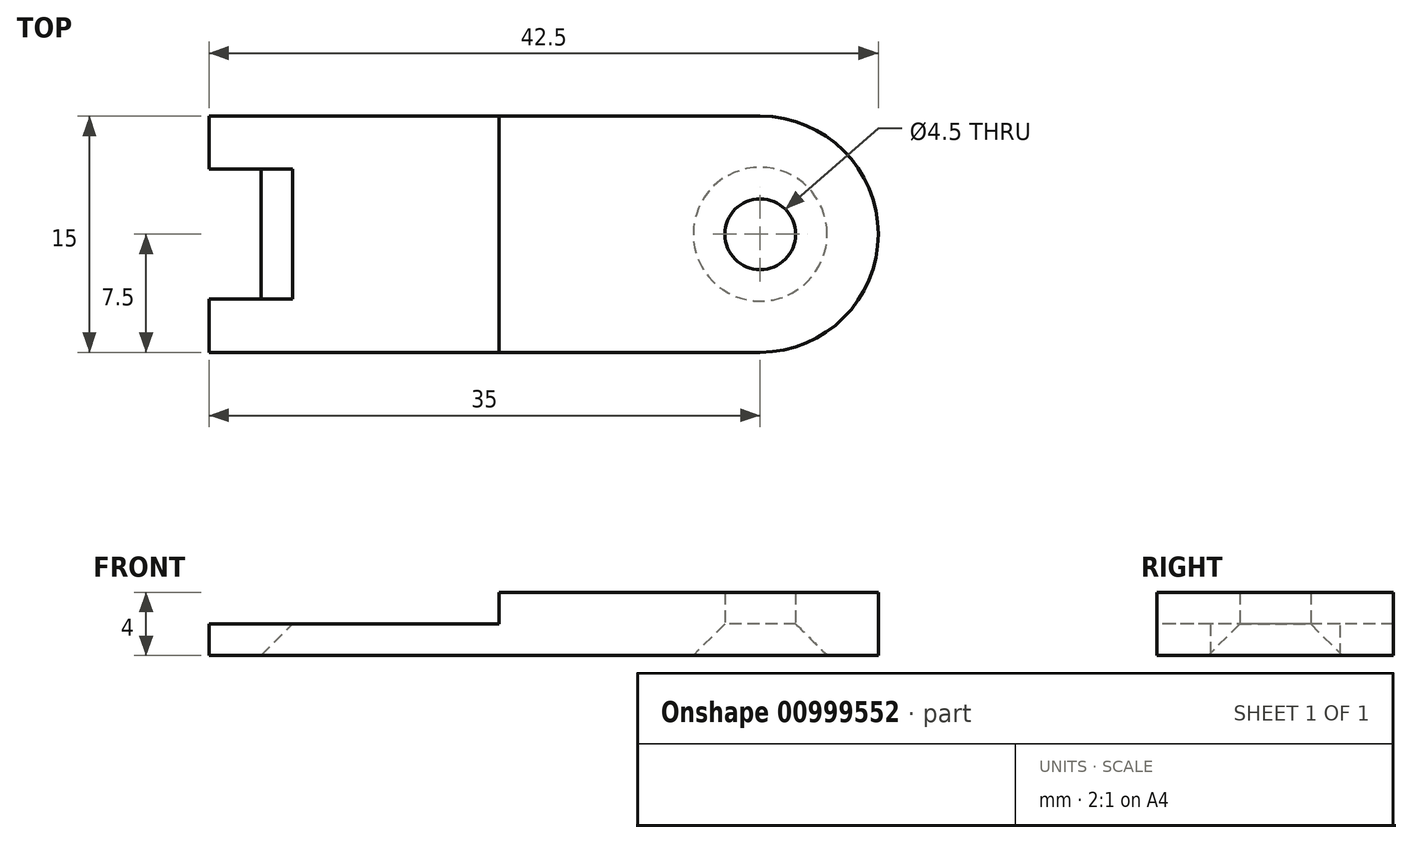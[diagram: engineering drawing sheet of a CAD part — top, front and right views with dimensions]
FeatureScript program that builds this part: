
annotation { "Feature Type Name" : "Feature", "Feature Type Description" : "" }
export const myFeature = defineFeature(function(context is Context, id is Id, definition is map)
    precondition{}
    {
        {
            var Q0;
            Q0=qCreatedBy(makeId("Top.planeOp"),FACE);
            var sketch = newSketch(context, id + "F0", { "sketchPlane" : qUnion([Q0])});
            skLineSegment(sketch, "E0.bottom", {"start": v(-21, 7.5) * mm, "end": v(14, 7.5) * mm});
            skLineSegment(sketch, "E0.top", {"start": v(-21, -7.5) * mm, "end": v(14, -7.5) * mm});
            skLineSegment(sketch, "E0.left", {"start": v(-21, 7.5) * mm, "end": v(-21, 4.12) * mm});
            skPoint(sketch, "E0.middle", {"position": v(0, 0) * mm});
            skCircle(sketch, "E1", {"center": v(14, 0) * mm, "radius": 2.25 * mm});
            skLineSegment(sketch, "E2.bottom", {"start": v(-17.7, 4.12) * mm, "end": v(-21, 4.12) * mm});
            skLineSegment(sketch, "E2.top", {"start": v(-17.7, -4.12) * mm, "end": v(-24.3, -4.12) * mm});
            skLineSegment(sketch, "E2.left", {"start": v(-17.7, 4.12) * mm, "end": v(-17.7, -4.13) * mm});
            skPoint(sketch, "E2.middle", {"position": v(-21, 0) * mm});
            skLineSegment(sketch, "E3.bottom", {"start": v(-2.6, 7.5) * mm, "end": v(-21, 7.5) * mm});
            skLineSegment(sketch, "E3.top", {"start": v(-2.6, -7.5) * mm, "end": v(-21, -7.5) * mm});
            skLineSegment(sketch, "E3.left", {"start": v(-2.6, 7.5) * mm, "end": v(-2.6, -7.5) * mm});
            skPoint(sketch, "E2.right.start.orphan", {"position": v(-24.3, 4.12) * mm});
            skLineSegment(sketch, "E4.trimOffspring", {"start": v(-21, -4.12) * mm, "end": v(-21, -7.5) * mm});
            skPoint(sketch, "E3.right.start.orphan", {"position": v(-39.4, 7.5) * mm});
            skPoint(sketch, "E5.orphan", {"position": v(-39.4, -7.5) * mm});
            skPoint(sketch, "E6.orphan", {"position": v(-2.6, 0) * mm});
            skArc(sketch, "E7", {"start": v(14, -7.5) * mm, "mid": v(21.5, 0) * mm, "end": v(14, 7.5) * mm});
            skPoint(sketch, "E8.orphan", {"position": v(21, 7.5) * mm});
            skPoint(sketch, "E9.orphan", {"position": v(21, -7.5) * mm});
            skSolve(sketch);
        }
        {
            var Q0;
            Q0=makeQuery(id+"F0.imprint","IMPRINT",FACE,{"disambiguationData":[TD([[makeQuery(id+"F0.imprint","IMPRINT",EDGE,{"derivedFrom":sQuery(id+"F0.wireOp",EDGE,"E0.bottom")}),-1.0]])]});
            extrude(context, id + "F1", {"entities" : qUnion([Q0]), "depth" : 4 * mm, "offsetDistance" : 25 * mm});
        }
        {
            var Q0;
            Q0=makeQuery(id+"F0.imprint","IMPRINT",FACE,{"disambiguationData":[TD([[makeQuery(id+"F0.imprint","IMPRINT",EDGE,{"derivedFrom":sQuery(id+"F0.wireOp",EDGE,"E0.left")}),1.0]])]});
            extrude(context, id + "F2", {"entities" : qUnion([Q0]), "operationType" : NewBodyOperationType.ADD, "depth" : 2 * mm, "offsetDistance" : 25 * mm});
        }
        {
            var Q0;
            Q0=makeQuery(id+"F1.opExtrude","CAP_EDGE",EDGE,{"disambiguationData":[OSD([sQuery(id+"F0.wireOp",EDGE,"E1")])],"isStart":true});
            var Q1;
            Q1=makeQuery(id+"F2.opExtrude","CAP_EDGE",EDGE,{"disambiguationData":[OSD([sQuery(id+"F0.wireOp",EDGE,"E2.left")])],"isStart":false});
            chamfer(context, id + "F3", {"entities" : qUnion([Q0, Q1]), "width" : 2 * mm, "tangentPropagation" : true});
        }
    });
